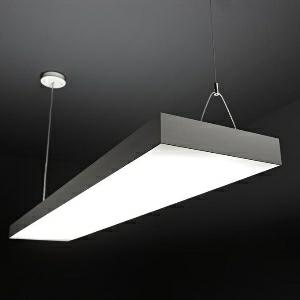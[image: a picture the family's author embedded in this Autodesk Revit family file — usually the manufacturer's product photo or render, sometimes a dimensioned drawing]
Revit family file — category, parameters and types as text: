
# Revit family: spectral_norea_norea-p_560_4590_840_mps_f02e
name_source: partatom
category: Lighting Fixtures
revit_build: Autodesk Revit 2016 (Build: 20150220_1215(x64)
units: mm (PartAtom-declared; Revit-internal decimal feet)

## family parameters
Cut with Voids When Loaded = No
Host = Face
Light Source = No
Part Type = Normal
Room Calculation Point = No
Round Connector Dimension = Use Diameter
Shared = No

## types (1)
- SPECTRAL NOREA (1 x )
    Apparent Load = 0 VA
    Approval mark = CE
    CIE Flux Codes = 72 93 98 75 75
    Control Gear = Electronic transformer
    Default Elevation = 1800 mm
    Description = SPT0000091
NOREA Pendant luminaire

Design:
Square luminaire element with a microprism panel in a natural anodised aluminium profile frame surround. The luminaire is suspended by a wire pendant with ceiling holder and transparent connecting cable with rectangular powder-coated ceiling junction box. Cable length adjustable at the junction box, steel wire steplessly height adjustable at the luminaire. The electrical gear is accommodated under a cover at the top of the luminaire. This can be removed using key holes for maintenance work. The indirect component for brightening the ceiling is provided by LED linear modules at the top of the luminaire. The LED module is formed as a rectangular LED flat board. Luminaire with heat-resistant wiring. Variant suitable for office use with a microprism panel MPS. The LED points are visible as circles on the microprism panel. Also in a dimmable version.

Colour:
Housing – similar to RAL 9016 White silk matt;
Frame – natural anodised
    Height = 50 mm
    Lamp = 1 x
    Lamp count = 1
    Length = 560 mm
    Luminous efficacy = 0 lm/W
    Manufacturer = Ridi
    ModVariant = No
    Model = NOREA-P 560/4590/840 MPS
    Mounting Place = Ceiling
    Mounting Type = Pendant
    Number of Poles = 1
    OnlyDefault = Yes
    Power Factor = 1
    Product Name = SPECTRAL NOREA
    Product group = Pendant luminaire
    ProductGroupID = 9
    Protection Class = Protection class
    Protection Degree = IP 20
    RlxData = <blob elided: 40697 chars, md5=c200855d>
    Socket = socket
    Standby Power = 0 W
    System Light Flux = 0 lm
    System Power = 0 W
    Type Image = norea01.jpg
    URL = http://reluxnet.relux.com
    VarID = 1
    Voltage = 0 V
    Weight = 0.00 kg
    Width = 312 mm

## geometry (parser evidence)
native form markers: Sweep x11
no freeform markers — native parametric forms only
